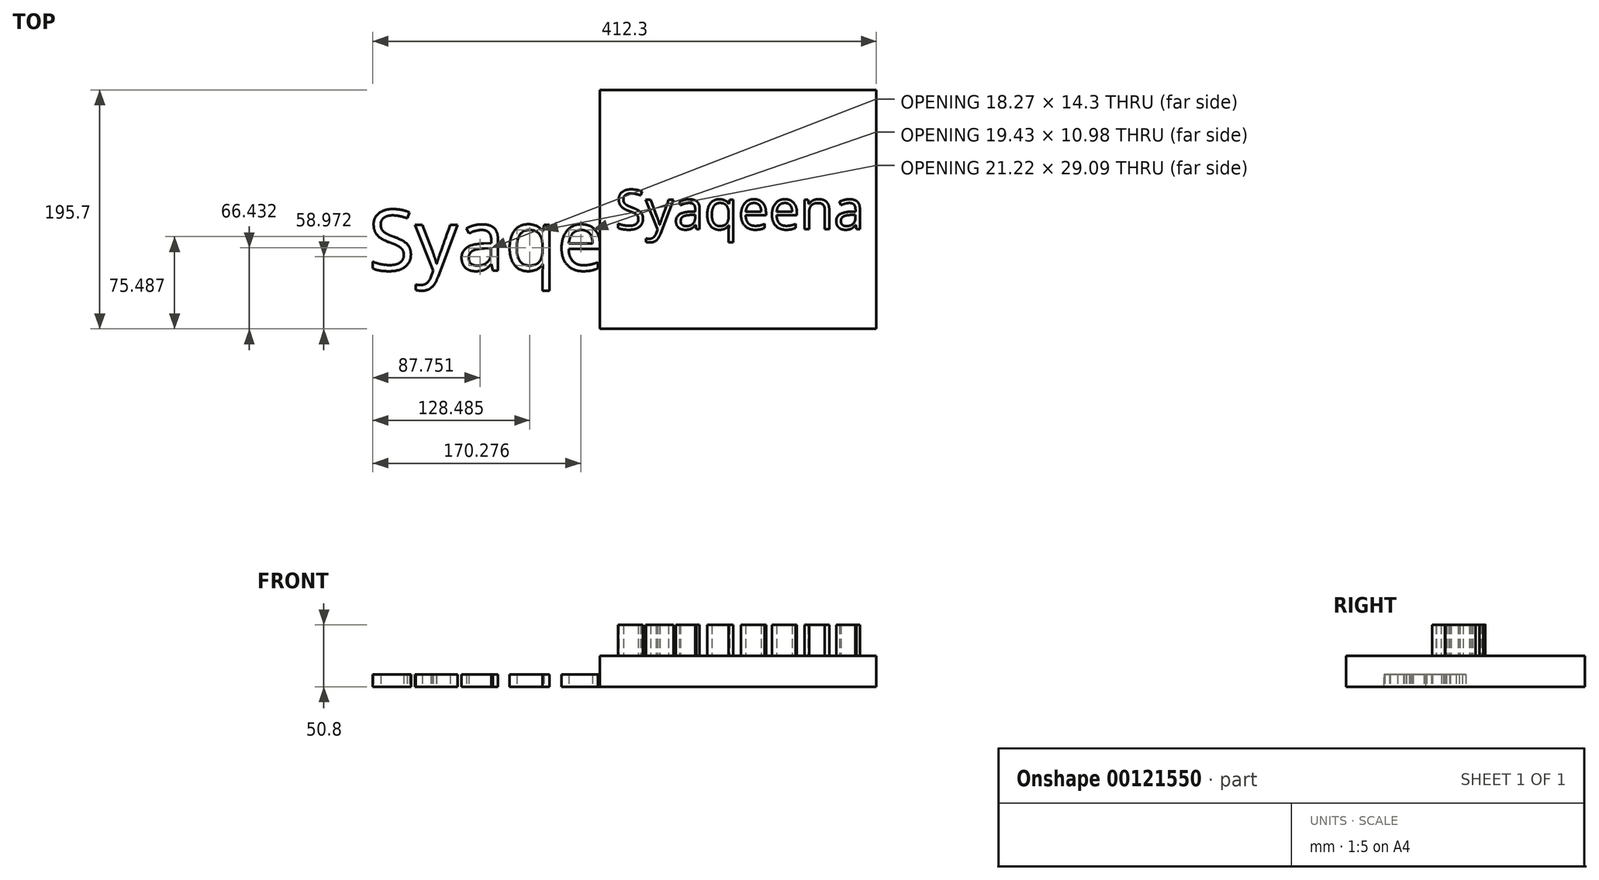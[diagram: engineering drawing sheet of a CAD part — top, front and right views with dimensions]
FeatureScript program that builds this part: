
annotation { "Feature Type Name" : "Feature", "Feature Type Description" : "" }
export const myFeature = defineFeature(function(context is Context, id is Id, definition is map)
    precondition{}
    {
        {
            var Q0;
            Q0=qCreatedBy(makeId("Top.planeOp"),FACE);
            var sketch = newSketch(context, id + "F0", { "sketchPlane" : qUnion([Q0])});
            skLineSegment(sketch, "E0.bottom", {"start": v(100, -50) * mm, "end": v(-100, -50) * mm});
            skLineSegment(sketch, "E0.top", {"start": v(100, 50) * mm, "end": v(-100, 50) * mm});
            skLineSegment(sketch, "E0.left", {"start": v(100, -50) * mm, "end": v(100, 50) * mm});
            skLineSegment(sketch, "E0.right", {"start": v(-100, -50) * mm, "end": v(-100, 50) * mm});
            skPoint(sketch, "E0.middle", {"position": v(0, 0) * mm});
            skText(sketch, "E1", { "text": "Syaqeena", "fontName": "OpenSans-Regular.ttf"});
            const initialGuessF0  = {"E1": [-0.30272, -0.05, 1, 0, 0.05]};
            skSetInitialGuess(sketch, initialGuessF0);
            skSolve(sketch);
        }
        {
            var Q0;
            Q0 = qSketchRegion(id + "F0", true);
            extrude(context, id + "F1", {"entities" : qUnion([Q0]), "depth" : 10 * mm});
        }
        {
            var Q0;
            Q0=qCreatedBy(makeId("Top.planeOp"),FACE);
            var sketch = newSketch(context, id + "F2", { "sketchPlane" : qUnion([Q0])});
            skLineSegment(sketch, "E2.bottom", {"start": v(113.17, 97.85) * mm, "end": v(-113.17, 97.85) * mm});
            skLineSegment(sketch, "E2.top", {"start": v(113.17, -97.85) * mm, "end": v(-113.17, -97.85) * mm});
            skLineSegment(sketch, "E2.left", {"start": v(113.17, 97.85) * mm, "end": v(113.17, -97.85) * mm});
            skLineSegment(sketch, "E2.right", {"start": v(-113.17, 97.85) * mm, "end": v(-113.17, -97.85) * mm});
            skPoint(sketch, "E2.middle", {"position": v(0, 0) * mm});
            skSolve(sketch);
        }
        {
            var Q0;
            Q0 = qSketchRegion(id + "F2", true);
            extrude(context, id + "F3", {"entities" : qUnion([Q0]), "operationType" : NewBodyOperationType.ADD, "depth" : 25.4 * mm});
        }
        {
            var Q0;
            Q0=makeQuery(id+"F3.opExtrude","CAP_FACE",FACE,{"disambiguationData":[OSD([sQuery(id+"F2.wireOp",EDGE,"E2.bottom"),sQuery(id+"F2.wireOp",EDGE,"E2.top"),sQuery(id+"F2.wireOp",EDGE,"E2.left"),sQuery(id+"F2.wireOp",EDGE,"E2.right")])],"isStart":false});
            var sketch = newSketch(context, id + "F4", { "sketchPlane" : qUnion([Q0])});
            skText(sketch, "E3", { "text": "Syaqeena", "fontName": "OpenSans-Regular.ttf"});
            const initialGuessF4  = {"E3": [-0.10047, -0.01628, 1, 0, 0.03253]};
            skSetInitialGuess(sketch, initialGuessF4);
            skSolve(sketch);
        }
        {
            var Q0;
            Q0 = qSketchRegion(id + "F4", true);
            extrude(context, id + "F5", {"entities" : qUnion([Q0]), "operationType" : NewBodyOperationType.ADD, "depth" : 25.4 * mm});
        }
    });
